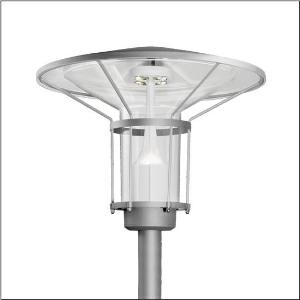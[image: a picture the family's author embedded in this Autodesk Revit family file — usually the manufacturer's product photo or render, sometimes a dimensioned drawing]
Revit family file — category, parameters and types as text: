
# Revit family: laterne_classic_iq___p1_0a_5xa5245ff14h000022_892e
name_source: partatom
category: Lighting Fixtures
units: mm (PartAtom-declared; Revit-internal decimal feet)

## family parameters
Cut with Voids When Loaded = No
Host = Face
Light Source = No
Part Type = Normal
Room Calculation Point = No
Round Connector Dimension = Use Diameter
Shared = No

## types (1)
- --- (1 x LED, 1360 lm, 10.5 W, 3000K)
    Apparent Load = 11 VA
    CIE Flux Codes = 30 61 91 96 100
    Color Rendering = 70
    Color Temperature = 3000K
    Default Elevation = 1800 mm
    Description = Lantern Classic iQ, mast luminaire, Module 540 iQ-SR, primary light control with 3 zone facetted reflector, of plastic, silver coated, highly specular, structured, primary optical cover: cover, of PMMA, transparent, light distribution: P1.0a, light emission: direct distribution, primary light characteristic: strongly asymmetric, installation type: post-top, LED, High Power LED, rated luminous flux: 1.360lm, luminous efficacy: 130lm/W, light colour: 730, colour temperature: 3000K, control gear: ECG iQ, control: Street-Remote, Auto-Match, Temp-Guard, Lumen-Switch, Night-Set, Smart-Wire, Light-Fading, Desk-Remote (wireless, voltage-free reading and setting of iQ features in the workshop via application-optimized NFC function/RFID function), optimised constant luminous flux control (CLO 2.0), pre-setting: logarithmic dimming characteristic, mains connection: 230..240V, AC, 50/60Hz, connection cable pre-assembled, cable length: 5,5m, wiring characteristics: H07RN-F, start of lifetime: 11W, end of service life: 11W, reduction: 5W, luminaire housing, upper part, of glass-fibre reinforced polyester, coated, Siteco® metallic grey (DB 702S), diameter: 750mm, height: 596mm, spigot size: d x l = 76 x 70mm (post-top) | with reducer (optional accessory) 60 x 70mm, post-top mast mounting element, of diecast aluminium, coated, Siteco® metallic grey (DB 702S), Module 540 iQ-SR, traffic white (RAL 9016), equipment: standard, protection rating (complete): IP65, insulation class (complete): insulation class II (safety insulation), certification: CE, ENEC, VDE, packaging unit: 1 piece

Light Distribution: P1.0a
    Height = 596 mm
    Lamp = 1 x LED
    Lamp Light Flux = 1360 lm
    Lamp Power = 10.5 W
    Lamp count = 1
    Length = 750 mm
    Luminous efficacy = 130 lm/W
    Manufacturer = Siteco
    ModVariant = No
    Model = 5XA5245FF14H000022
    Number of Poles = 1
    OnlyDefault = Yes
    Power Factor = 1
    Product Name = Laterne Classic iQ | P1.0a
    Product group = mast luminaire | pylon top
    ProductGroupID = 6100
    Protection Class = Protection class II
    Protection Degree = IP 65
    RLX_Detail_Level = 1
    RLX_Emergency_Light_Flux = 0 lm
    RLX_Emergency_Type = 0
    RLX_Emergency_Type_DB = No
    RlxData = <blob elided: 64533 chars, md5=6a8aaccd>
    Socket = socket
    Standby Power = 0 W
    System Light Flux = 1360 lm
    System Power = 11 W
    Type Comments = factory setting: luminous flux: 100 % | dim-lin: 254 | 419 mA
    Type Image = l_1006052.jpg
    URL = http://relux.com
    VarID = @adj_130539
    Voltage = 0 V
    Weight = 0.00 kg
    Width = 0 mm  [stored 0 ft]

note: [stored X ft] marks values corroborated as IEEE doubles in the binary element streams (Revit-internal decimal feet)

## geometry (parser evidence)
native form markers: Blend x4, Sweep x8
no freeform markers — native parametric forms only
